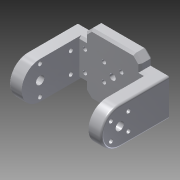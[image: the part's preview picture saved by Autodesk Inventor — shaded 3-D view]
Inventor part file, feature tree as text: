
AUTODESK INVENTOR PART (.ipt)
format: ipt  version: 2015 (Build 190159000, 159)  size: 320,512 bytes
history: native  units: mm
features: sketch x11, hole x7, extrude x4, chamfer x3, fillet x2, pattern_circular x2, other x1
ambient origin geometry x8: Origin, YZ Plane, XZ Plane, XY Plane, X Axis, Y Axis, Z Axis, Center Point
bodies: Body1 (feature_tree)
feature tree (30):
  other  "ソリッド1"
  extrude  "押し出し1"  Depth=45.0mm
  extrude  "押し出し2"  Depth=34.0mm
  hole  "穴1"  [1 undecoded]
  fillet  "フィレット1"  Radius=6.25mm
  fillet  "フィレット2"  Radius=6.25mm
  hole  "穴2"  [1 undecoded]
  hole  "穴4"  [1 undecoded]
  pattern_circular  "円形状パターン1"  [2 undecoded]
  extrude  "押し出し3"  Depth=25.0mm
  extrude  "押し出し4"  Depth=9.0mm
  chamfer  "面取り1"  Distance=1.0mm
  chamfer  "面取り2"  Distance=6.0mm
  hole  "穴5"  [1 undecoded]
  hole  "穴6"  [1 undecoded]
  hole  "穴7"  [1 undecoded]
  hole  "穴8"  [1 undecoded]
  pattern_circular  "円形状パターン2"  [2 undecoded]
  chamfer  "面取り3"  [1 undecoded]
  sketch  "スケッチ1"
  sketch  "スケッチ2"
  sketch  "スケッチ4"
  sketch  "スケッチ5"
  sketch  "スケッチ7"
  sketch  "スケッチ8"
  sketch  "スケッチ9"
  sketch  "スケッチ10"
  sketch  "スケッチ11"
  sketch  "スケッチ12"
  sketch  "スケッチ13"
note: 12 required parameter values undecoded (feature->parameter linkage not recoverable at this tier; creation-order binding heuristic only, values carry confidence <= 0.55)
